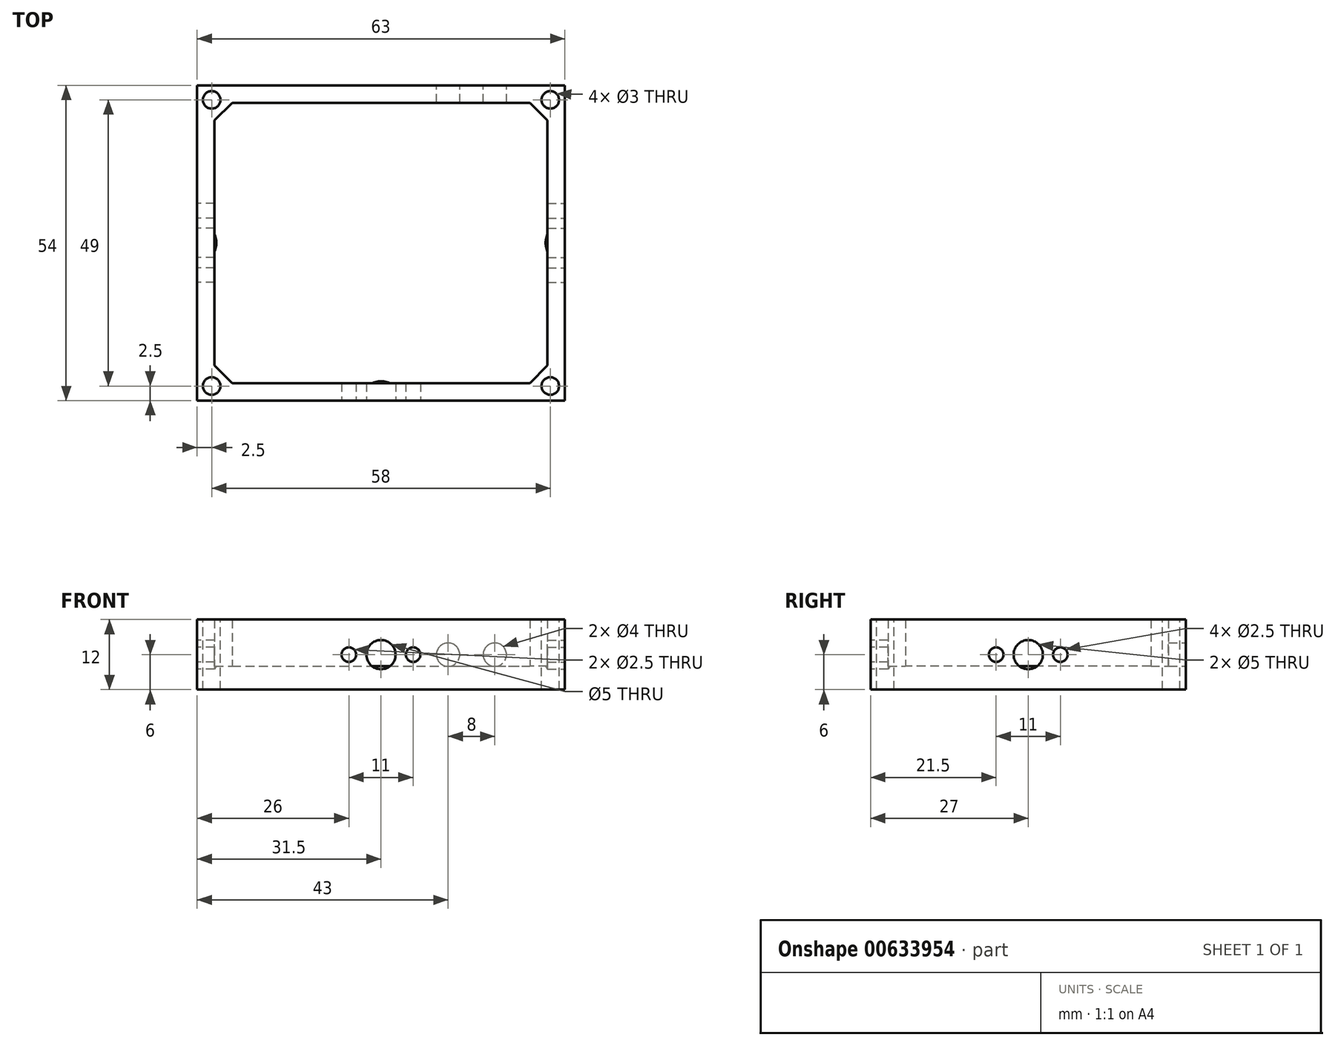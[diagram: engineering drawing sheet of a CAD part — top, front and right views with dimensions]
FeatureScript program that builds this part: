
annotation { "Feature Type Name" : "Feature", "Feature Type Description" : "" }
export const myFeature = defineFeature(function(context is Context, id is Id, definition is map)
    precondition{}
    {
        {
            var Q0;
            Q0=qCreatedBy(makeId("Top.planeOp"),FACE);
            var sketch = newSketch(context, id + "F0", { "sketchPlane" : qUnion([Q0])});
            skLineSegment(sketch, "E0.bottom", {"start": v(0, 0) * mm, "end": v(63, 0) * mm});
            skLineSegment(sketch, "E0.top", {"start": v(0, 54) * mm, "end": v(63, 54) * mm});
            skLineSegment(sketch, "E0.left", {"start": v(0, 0) * mm, "end": v(0, 54) * mm});
            skLineSegment(sketch, "E0.right", {"start": v(63, 0) * mm, "end": v(63, 54) * mm});
            skSolve(sketch);
        }
        {
            var Q0;
            Q0=makeQuery(id+"F0.imprint","IMPRINT",FACE,{"disambiguationData":[TD([[makeQuery(id+"F0.imprint","IMPRINT",EDGE,{"derivedFrom":sQuery(id+"F0.wireOp",EDGE,"E0.bottom")}),1.0]])]});
            extrude(context, id + "F1", {"entities" : qUnion([Q0]), "depth" : 4 * mm, "offsetDistance" : 25 * mm});
        }
        {
            var Q0;
            Q0=makeQuery(id+"F1.opExtrude","CAP_FACE",FACE,{"disambiguationData":[OSD([sQuery(id+"F0.wireOp",EDGE,"E0.bottom"),sQuery(id+"F0.wireOp",EDGE,"E0.top"),sQuery(id+"F0.wireOp",EDGE,"E0.left"),sQuery(id+"F0.wireOp",EDGE,"E0.right")])],"isStart":false});
            var sketch = newSketch(context, id + "F2", { "sketchPlane" : qUnion([Q0])});
            skLineSegment(sketch, "E1.bottom", {"start": v(6, 51) * mm, "end": v(57, 51) * mm});
            skLineSegment(sketch, "E1.top", {"start": v(6, 3) * mm, "end": v(57, 3) * mm});
            skLineSegment(sketch, "E1.left", {"start": v(3, 48) * mm, "end": v(3, 6) * mm});
            skLineSegment(sketch, "E1.right", {"start": v(60, 48) * mm, "end": v(60, 6) * mm});
            skLineSegment(sketch, "E2", {"start": v(3, 48) * mm, "end": v(6, 51) * mm});
            skPoint(sketch, "E3.orphan", {"position": v(3, 51) * mm});
            skLineSegment(sketch, "E4", {"start": v(6, 3) * mm, "end": v(3, 6) * mm});
            skLineSegment(sketch, "E5", {"start": v(57, 3) * mm, "end": v(60, 6) * mm});
            skLineSegment(sketch, "E6", {"start": v(60, 48) * mm, "end": v(57, 51) * mm});
            skPoint(sketch, "E7.orphan", {"position": v(3, 3) * mm});
            skPoint(sketch, "E8.orphan", {"position": v(60, 3) * mm});
            skPoint(sketch, "E9.orphan", {"position": v(60, 51) * mm});
            skLineSegment(sketch, "E10.bottom", {"start": v(0, 54) * mm, "end": v(63, 54) * mm});
            skLineSegment(sketch, "E10.top", {"start": v(0, 0) * mm, "end": v(63, 0) * mm});
            skLineSegment(sketch, "E10.left", {"start": v(0, 54) * mm, "end": v(0, 0) * mm});
            skLineSegment(sketch, "E10.right", {"start": v(63, 54) * mm, "end": v(63, 0) * mm});
            skSolve(sketch);
        }
        {
            var Q0;
            Q0=makeQuery(id+"F2.imprint","IMPRINT",FACE,{"disambiguationData":[TD([[makeQuery(id+"F2.imprint","IMPRINT",EDGE,{"derivedFrom":sQuery(id+"F2.wireOp",EDGE,"E1.bottom")}),1.0]])]});
            extrude(context, id + "F3", {"entities" : qUnion([Q0]), "operationType" : NewBodyOperationType.ADD, "depth" : 8 * mm, "offsetDistance" : 25 * mm});
        }
        {
            var Q0;
            Q0=makeQuery(id+"F3.boolean.opBoolean","MERGE",FACE,{"derivedFrom":[makeQuery(id+"F1.opExtrude","SWEPT_FACE",FACE,{"disambiguationData":[OSD([sQuery(id+"F0.wireOp",EDGE,"E0.bottom")])]}),makeQuery(id+"F3.opExtrude","SWEPT_FACE",FACE,{"disambiguationData":[OSD([sQuery(id+"F2.wireOp",EDGE,"E10.top")])]})]});
            var sketch = newSketch(context, id + "F4", { "sketchPlane" : qUnion([Q0])});
            skLineSegment(sketch, "E11", {"start": v(0, 6) * mm, "end": v(63, 6) * mm, "construction": true});
            skCircle(sketch, "E12", {"center": v(26, 6) * mm, "radius": 1.25 * mm});
            skLineSegment(sketch, "E13", {"start": v(31.5, 12) * mm, "end": v(31.5, 0) * mm, "construction": true});
            skCircle(sketch, "E14.MirrorC", {"center": v(37, 6) * mm, "radius": 1.25 * mm});
            skSolve(sketch);
        }
        {
            var Q0;
            Q0=makeQuery(id+"F3.boolean.opBoolean","MERGE",FACE,{"derivedFrom":[makeQuery(id+"F1.opExtrude","SWEPT_FACE",FACE,{"disambiguationData":[OSD([sQuery(id+"F0.wireOp",EDGE,"E0.right")])]}),makeQuery(id+"F3.opExtrude","SWEPT_FACE",FACE,{"disambiguationData":[OSD([sQuery(id+"F2.wireOp",EDGE,"E10.right")])]})]});
            var sketch = newSketch(context, id + "F5", { "sketchPlane" : qUnion([Q0])});
            skLineSegment(sketch, "E15", {"start": v(0, 6) * mm, "end": v(54, 6) * mm, "construction": true});
            skCircle(sketch, "E16", {"center": v(21.5, 6) * mm, "radius": 1.25 * mm});
            skLineSegment(sketch, "E17", {"start": v(27, 12) * mm, "end": v(27, 0) * mm, "construction": true});
            skCircle(sketch, "E18.MirrorC", {"center": v(32.5, 6) * mm, "radius": 1.25 * mm});
            skSolve(sketch);
        }
        {
            var Q0;
            Q0=makeQuery(id+"F3.boolean.opBoolean","MERGE",FACE,{"derivedFrom":[makeQuery(id+"F1.opExtrude","SWEPT_FACE",FACE,{"disambiguationData":[OSD([sQuery(id+"F0.wireOp",EDGE,"E0.top")])]}),makeQuery(id+"F3.opExtrude","SWEPT_FACE",FACE,{"disambiguationData":[OSD([sQuery(id+"F2.wireOp",EDGE,"E10.bottom")])]})]});
            var sketch = newSketch(context, id + "F6", { "sketchPlane" : qUnion([Q0])});
            skLineSegment(sketch, "E19", {"start": v(-63, 6) * mm, "end": v(0, 6) * mm, "construction": true});
            skLineSegment(sketch, "E20", {"start": v(-31.5, 12) * mm, "end": v(-31.5, 0) * mm, "construction": true});
            skCircle(sketch, "E21", {"center": v(-43, 6) * mm, "radius": 2 * mm});
            skCircle(sketch, "E22", {"center": v(-51, 6) * mm, "radius": 2 * mm});
            skSolve(sketch);
        }
        {
            var Q0;
            Q0 = qSketchRegion(id + "F6", true);
            extrude(context, id + "F7", {"entities" : qUnion([Q0]), "operationType" : NewBodyOperationType.REMOVE, "oppositeDirection" : true, "depth" : 3 * mm, "offsetDistance" : 25 * mm});
        }
        {
            var Q0;
            Q0=sQuery(id+"F4.wireOp",VERTEX,"E12.center");
            var Q1;
            Q1=sQuery(id+"F4.wireOp",VERTEX,"E14.MirrorC.center");
            var Q2;
            Q2=makeQuery(id+"F1.opExtrude","SWEPT_BODY",BODY,{"disambiguationData":[OSD([sQuery(id+"F0.wireOp",EDGE,"E0.bottom"),sQuery(id+"F0.wireOp",EDGE,"E0.top"),sQuery(id+"F0.wireOp",EDGE,"E0.left"),sQuery(id+"F0.wireOp",EDGE,"E0.right")])]});
            hole(context, id + "F8", {"style" : HoleStyle.SIMPLE, "endStyle" : HoleEndStyle.BLIND, "standardTappedOrClearance" : lookupTablePath({ "standard" : "ISO", "engagement" : "75%", "pitch" : "0.5 mm", "size" : "M3", "type" : "Tapped" }), "standardBlindInLast" : lookupTablePath({ "standard" : "ISO", "engagement" : "75%", "pitch" : "0.5 mm", "size" : "M3", "type" : "Tapped" }), "holeDiameter" : 2.5 * mm, "majorDiameter" : 3 * mm, "showTappedDepth" : true, "holeDepth" : 4.5 * mm, "isTappedThrough" : true, "tappedDepth" : 3 * mm, "tapClearance" : 3, "startFromSketch" : true, "locations" : qUnion([Q0, Q1]), "scope" : qUnion([Q2])});
        }
        {
            var Q0;
            Q0=makeQuery(id+"F3.boolean.opBoolean","MERGE",FACE,{"derivedFrom":[makeQuery(id+"F1.opExtrude","SWEPT_FACE",FACE,{"disambiguationData":[OSD([sQuery(id+"F0.wireOp",EDGE,"E0.left")])]}),makeQuery(id+"F3.opExtrude","SWEPT_FACE",FACE,{"disambiguationData":[OSD([sQuery(id+"F2.wireOp",EDGE,"E10.left")])]})]});
            var sketch = newSketch(context, id + "F9", { "sketchPlane" : qUnion([Q0])});
            skLineSegment(sketch, "E23", {"start": v(-54, 6) * mm, "end": v(0, 6) * mm, "construction": true});
            skCircle(sketch, "E24", {"center": v(-32.5, 6) * mm, "radius": 1.25 * mm});
            skLineSegment(sketch, "E25", {"start": v(-27, 12) * mm, "end": v(-27, 0) * mm, "construction": true});
            skCircle(sketch, "E26.MirrorC", {"center": v(-21.5, 6) * mm, "radius": 1.25 * mm});
            skSolve(sketch);
        }
        {
            var Q0;
            Q0=sQuery(id+"F9.wireOp",VERTEX,"E24.center");
            var Q1;
            Q1=sQuery(id+"F9.wireOp",VERTEX,"E26.MirrorC.center");
            var Q2;
            Q2=makeQuery(id+"F1.opExtrude","SWEPT_BODY",BODY,{"disambiguationData":[OSD([sQuery(id+"F0.wireOp",EDGE,"E0.bottom"),sQuery(id+"F0.wireOp",EDGE,"E0.top"),sQuery(id+"F0.wireOp",EDGE,"E0.left"),sQuery(id+"F0.wireOp",EDGE,"E0.right")])]});
            hole(context, id + "F10", {"style" : HoleStyle.SIMPLE, "endStyle" : HoleEndStyle.BLIND, "standardTappedOrClearance" : lookupTablePath({ "standard" : "ISO", "engagement" : "75%", "pitch" : "0.5 mm", "size" : "M3", "type" : "Tapped" }), "standardBlindInLast" : lookupTablePath({ "standard" : "ISO", "engagement" : "75%", "pitch" : "0.5 mm", "size" : "M3", "type" : "Tapped" }), "holeDiameter" : 2.5 * mm, "majorDiameter" : 3 * mm, "showTappedDepth" : true, "holeDepth" : 4.5 * mm, "isTappedThrough" : true, "tappedDepth" : 3 * mm, "tapClearance" : 3, "startFromSketch" : true, "locations" : qUnion([Q0, Q1]), "scope" : qUnion([Q2])});
        }
        {
            var Q0;
            Q0=makeQuery(id+"F3.boolean.opBoolean","MERGE",FACE,{"derivedFrom":[makeQuery(id+"F1.opExtrude","SWEPT_FACE",FACE,{"disambiguationData":[OSD([sQuery(id+"F0.wireOp",EDGE,"E0.left")])]}),makeQuery(id+"F3.opExtrude","SWEPT_FACE",FACE,{"disambiguationData":[OSD([sQuery(id+"F2.wireOp",EDGE,"E10.left")])]})]});
            var sketch = newSketch(context, id + "F11", { "sketchPlane" : qUnion([Q0])});
            skLineSegment(sketch, "E27", {"start": v(-27, 0) * mm, "end": v(-27, 12) * mm, "construction": true});
            skPoint(sketch, "E28", {"position": v(-27, 6) * mm});
            skSolve(sketch);
        }
        {
            var Q0;
            Q0=sQuery(id+"F11.wireOp",VERTEX,"E28");
            var Q1;
            Q1=makeQuery(id+"F1.opExtrude","SWEPT_BODY",BODY,{"disambiguationData":[OSD([sQuery(id+"F0.wireOp",EDGE,"E0.bottom"),sQuery(id+"F0.wireOp",EDGE,"E0.top"),sQuery(id+"F0.wireOp",EDGE,"E0.left"),sQuery(id+"F0.wireOp",EDGE,"E0.right")])]});
            hole(context, id + "F12", {"style" : HoleStyle.SIMPLE, "endStyle" : HoleEndStyle.BLIND, "standardTappedOrClearance" : lookupTablePath({ "standard" : "ISO", "size" : "5", "type" : "Drilled" }), "standardBlindInLast" : lookupTablePath({ "standard" : "ISO", "size" : "5", "type" : "Drilled" }), "holeDiameter" : 5 * mm, "majorDiameter" : 6 * mm, "holeDepth" : 3 * mm, "isTappedThrough" : true, "tappedDepth" : 3 * mm, "tapClearance" : 3, "startFromSketch" : true, "locations" : qUnion([Q0]), "scope" : qUnion([Q1])});
        }
        {
            var Q0;
            Q0=makeQuery(id+"F3.boolean.opBoolean","MERGE",FACE,{"derivedFrom":[makeQuery(id+"F1.opExtrude","SWEPT_FACE",FACE,{"disambiguationData":[OSD([sQuery(id+"F0.wireOp",EDGE,"E0.bottom")])]}),makeQuery(id+"F3.opExtrude","SWEPT_FACE",FACE,{"disambiguationData":[OSD([sQuery(id+"F2.wireOp",EDGE,"E10.top")])]})]});
            var sketch = newSketch(context, id + "F13", { "sketchPlane" : qUnion([Q0])});
            skLineSegment(sketch, "E29", {"start": v(31.5, 12) * mm, "end": v(31.5, 0) * mm, "construction": true});
            skPoint(sketch, "E30", {"position": v(31.5, 6) * mm});
            skSolve(sketch);
        }
        {
            var Q0;
            Q0=sQuery(id+"F13.wireOp",VERTEX,"E30");
            var Q1;
            Q1=makeQuery(id+"F1.opExtrude","SWEPT_BODY",BODY,{"disambiguationData":[OSD([sQuery(id+"F0.wireOp",EDGE,"E0.bottom"),sQuery(id+"F0.wireOp",EDGE,"E0.top"),sQuery(id+"F0.wireOp",EDGE,"E0.left"),sQuery(id+"F0.wireOp",EDGE,"E0.right")])]});
            hole(context, id + "F14", {"style" : HoleStyle.SIMPLE, "endStyle" : HoleEndStyle.BLIND, "standardTappedOrClearance" : lookupTablePath({ "standard" : "ISO", "size" : "5", "type" : "Drilled" }), "standardBlindInLast" : lookupTablePath({ "standard" : "ISO", "size" : "5", "type" : "Drilled" }), "holeDiameter" : 5 * mm, "majorDiameter" : 5 * mm, "holeDepth" : 3 * mm, "isTappedThrough" : true, "tappedDepth" : 3 * mm, "tapClearance" : 3, "startFromSketch" : true, "locations" : qUnion([Q0]), "scope" : qUnion([Q1])});
        }
        {
            var Q0;
            Q0=sQuery(id+"F5.wireOp",VERTEX,"E16.center");
            var Q1;
            Q1=sQuery(id+"F5.wireOp",VERTEX,"E18.MirrorC.center");
            var Q2;
            Q2=makeQuery(id+"F1.opExtrude","SWEPT_BODY",BODY,{"disambiguationData":[OSD([sQuery(id+"F0.wireOp",EDGE,"E0.bottom"),sQuery(id+"F0.wireOp",EDGE,"E0.top"),sQuery(id+"F0.wireOp",EDGE,"E0.left"),sQuery(id+"F0.wireOp",EDGE,"E0.right")])]});
            hole(context, id + "F15", {"style" : HoleStyle.SIMPLE, "endStyle" : HoleEndStyle.BLIND, "standardTappedOrClearance" : lookupTablePath({ "standard" : "ISO", "engagement" : "75%", "pitch" : "0.5 mm", "size" : "M3", "type" : "Tapped" }), "standardBlindInLast" : lookupTablePath({ "standard" : "ISO", "engagement" : "75%", "pitch" : "0.5 mm", "size" : "M3", "type" : "Tapped" }), "holeDiameter" : 2.5 * mm, "majorDiameter" : 3 * mm, "showTappedDepth" : true, "holeDepth" : 4.5 * mm, "isTappedThrough" : true, "tappedDepth" : 3 * mm, "tapClearance" : 3, "startFromSketch" : true, "locations" : qUnion([Q0, Q1]), "scope" : qUnion([Q2])});
        }
        {
            var Q0;
            Q0=makeQuery(id+"F3.boolean.opBoolean","MERGE",FACE,{"derivedFrom":[makeQuery(id+"F1.opExtrude","SWEPT_FACE",FACE,{"disambiguationData":[OSD([sQuery(id+"F0.wireOp",EDGE,"E0.right")])]}),makeQuery(id+"F3.opExtrude","SWEPT_FACE",FACE,{"disambiguationData":[OSD([sQuery(id+"F2.wireOp",EDGE,"E10.right")])]})]});
            var sketch = newSketch(context, id + "F16", { "sketchPlane" : qUnion([Q0])});
            skLineSegment(sketch, "E31", {"start": v(27, 0) * mm, "end": v(27, 12) * mm, "construction": true});
            skPoint(sketch, "E32", {"position": v(27, 6) * mm});
            skSolve(sketch);
        }
        {
            var Q0;
            Q0=sQuery(id+"F16.wireOp",VERTEX,"E32");
            var Q1;
            Q1=makeQuery(id+"F1.opExtrude","SWEPT_BODY",BODY,{"disambiguationData":[OSD([sQuery(id+"F0.wireOp",EDGE,"E0.bottom"),sQuery(id+"F0.wireOp",EDGE,"E0.top"),sQuery(id+"F0.wireOp",EDGE,"E0.left"),sQuery(id+"F0.wireOp",EDGE,"E0.right")])]});
            hole(context, id + "F17", {"style" : HoleStyle.SIMPLE, "endStyle" : HoleEndStyle.BLIND, "standardTappedOrClearance" : lookupTablePath({ "standard" : "ISO", "size" : "5", "type" : "Drilled" }), "standardBlindInLast" : lookupTablePath({ "standard" : "ISO", "size" : "5", "type" : "Drilled" }), "holeDiameter" : 5 * mm, "majorDiameter" : 3 * mm, "holeDepth" : 3 * mm, "isTappedThrough" : true, "tappedDepth" : 3 * mm, "tapClearance" : 3, "startFromSketch" : true, "locations" : qUnion([Q0]), "scope" : qUnion([Q1])});
        }
        {
            var Q0;
            Q0=makeQuery(id+"F3.opExtrude","CAP_FACE",FACE,{"disambiguationData":[OSD([sQuery(id+"F2.wireOp",EDGE,"E1.bottom"),sQuery(id+"F2.wireOp",EDGE,"E1.top"),sQuery(id+"F2.wireOp",EDGE,"E1.left"),sQuery(id+"F2.wireOp",EDGE,"E1.right"),sQuery(id+"F2.wireOp",EDGE,"E2"),sQuery(id+"F2.wireOp",EDGE,"E4"),sQuery(id+"F2.wireOp",EDGE,"E5"),sQuery(id+"F2.wireOp",EDGE,"E6"),sQuery(id+"F2.wireOp",EDGE,"E10.bottom"),sQuery(id+"F2.wireOp",EDGE,"E10.top"),sQuery(id+"F2.wireOp",EDGE,"E10.left"),sQuery(id+"F2.wireOp",EDGE,"E10.right")])],"isStart":false});
            var sketch = newSketch(context, id + "F18", { "sketchPlane" : qUnion([Q0])});
            skLineSegment(sketch, "E33.bottom", {"start": v(2.5, 51.5) * mm, "end": v(60.5, 51.5) * mm, "construction": true});
            skLineSegment(sketch, "E33.top", {"start": v(2.5, 2.5) * mm, "end": v(60.5, 2.5) * mm, "construction": true});
            skLineSegment(sketch, "E33.left", {"start": v(2.5, 51.5) * mm, "end": v(2.5, 2.5) * mm, "construction": true});
            skLineSegment(sketch, "E33.right", {"start": v(60.5, 51.5) * mm, "end": v(60.5, 2.5) * mm, "construction": true});
            skCircle(sketch, "E34", {"center": v(2.5, 51.5) * mm, "radius": 1.5 * mm});
            skCircle(sketch, "E35", {"center": v(60.5, 51.5) * mm, "radius": 1.5 * mm});
            skCircle(sketch, "E36", {"center": v(2.5, 2.5) * mm, "radius": 1.5 * mm});
            skCircle(sketch, "E37", {"center": v(60.5, 2.5) * mm, "radius": 1.5 * mm});
            skSolve(sketch);
        }
        {
            var Q0;
            Q0 = qSketchRegion(id + "F18", true);
            extrude(context, id + "F19", {"entities" : qUnion([Q0]), "operationType" : NewBodyOperationType.REMOVE, "oppositeDirection" : true, "depth" : 12 * mm, "offsetDistance" : 25 * mm});
        }
    });
